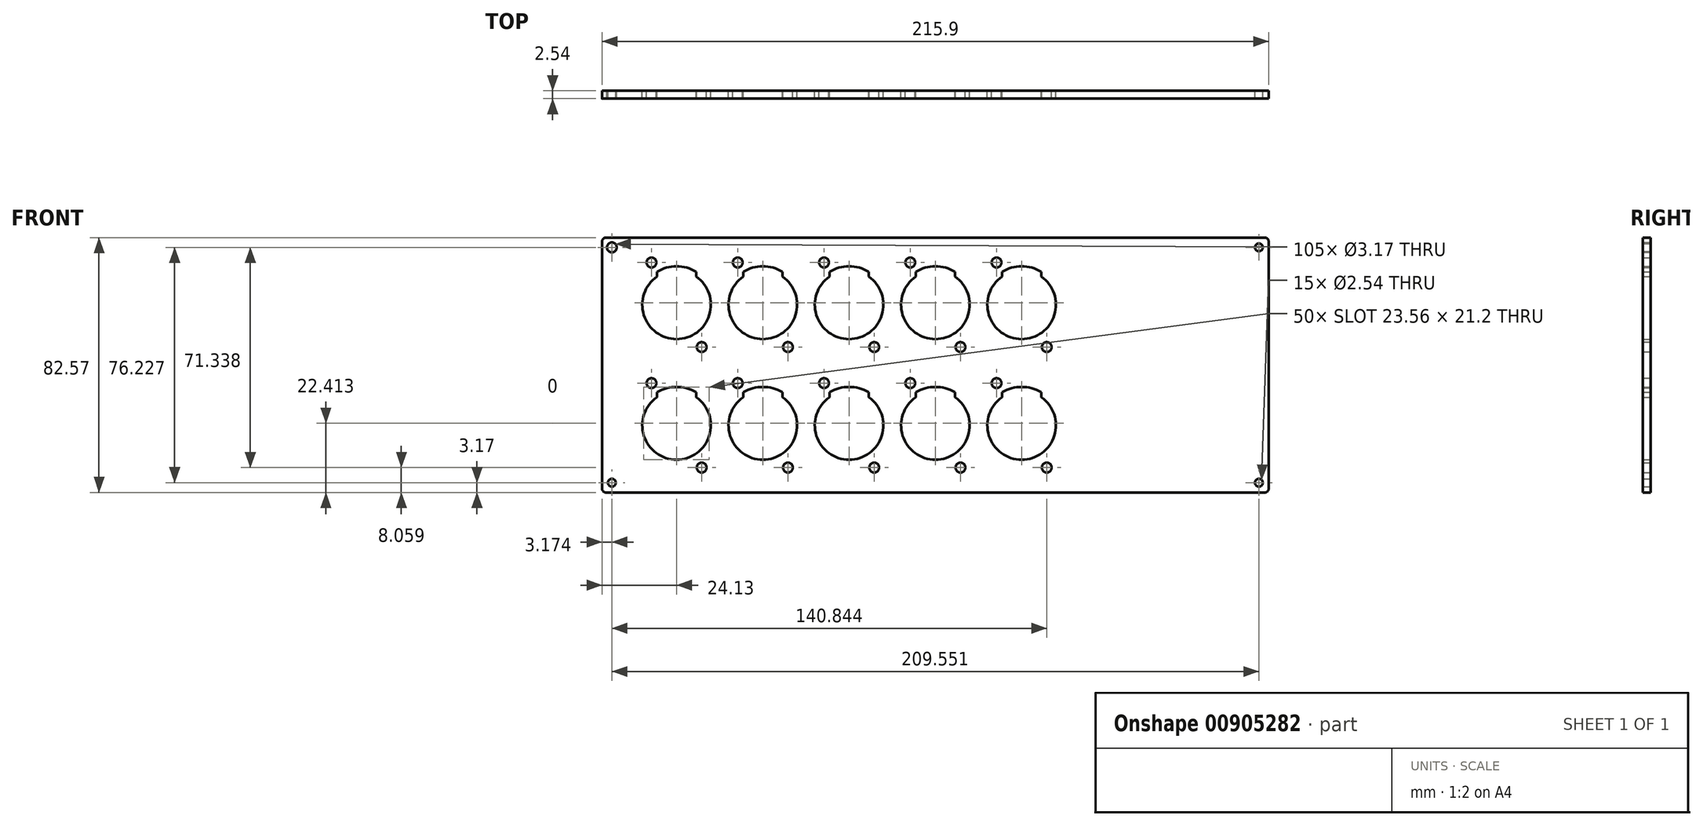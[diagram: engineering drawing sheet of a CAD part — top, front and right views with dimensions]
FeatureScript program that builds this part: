
annotation { "Feature Type Name" : "Feature", "Feature Type Description" : "" }
export const myFeature = defineFeature(function(context is Context, id is Id, definition is map)
    precondition{}
    {
        {
            var Q0;
            Q0=qCreatedBy(makeId("Front.planeOp"),FACE);
            var sketch = newSketch(context, id + "F0", { "sketchPlane" : qUnion([Q0])});
            skArc(sketch, "E0", {"start": v(-90.17, 28.65) * mm, "mid": v(-83.82, 8.41) * mm, "end": v(-77.47, 28.65) * mm});
            skPoint(sketch, "E0.centerSnap0", {"position": v(-71.12, 19.53) * mm});
            skPoint(sketch, "E0.centerSnap1", {"position": v(-83.82, 37.78) * mm});
            skCircle(sketch, "E1", {"center": v(-91.95, 33.21) * mm, "radius": 1.59 * mm});
            skCircle(sketch, "E2", {"center": v(-75.7, 5.84) * mm, "radius": 1.59 * mm});
            skArc(sketch, "E3", {"start": v(-77.47, 30.24) * mm, "mid": v(-83.82, 31.98) * mm, "end": v(-90.17, 30.24) * mm});
            skLineSegment(sketch, "E4", {"start": v(-90.17, 30.24) * mm, "end": v(-90.17, 28.65) * mm});
            skLineSegment(sketch, "E5", {"start": v(-77.47, 30.24) * mm, "end": v(-77.47, 28.65) * mm});
            skArc(sketch, "E6", {"start": v(-62.23, 28.65) * mm, "mid": v(-55.88, 8.41) * mm, "end": v(-49.53, 28.65) * mm});
            skPoint(sketch, "E6.centerSnap0", {"position": v(-43.18, 19.53) * mm});
            skPoint(sketch, "E6.centerSnap1", {"position": v(-55.88, 37.78) * mm});
            skCircle(sketch, "E7", {"center": v(-64, 33.21) * mm, "radius": 1.59 * mm});
            skCircle(sketch, "E8", {"center": v(-47.75, 5.84) * mm, "radius": 1.59 * mm});
            skArc(sketch, "E9", {"start": v(-49.53, 30.24) * mm, "mid": v(-55.88, 31.98) * mm, "end": v(-62.23, 30.24) * mm});
            skLineSegment(sketch, "E10", {"start": v(-62.23, 30.24) * mm, "end": v(-62.23, 28.65) * mm});
            skLineSegment(sketch, "E11", {"start": v(-49.53, 30.24) * mm, "end": v(-49.53, 28.65) * mm});
            skArc(sketch, "E12", {"start": v(-34.3, 28.65) * mm, "mid": v(-27.94, 8.41) * mm, "end": v(-21.59, 28.65) * mm});
            skPoint(sketch, "E12.centerSnap0", {"position": v(-15.24, 19.53) * mm});
            skPoint(sketch, "E12.centerSnap1", {"position": v(-27.94, 37.78) * mm});
            skCircle(sketch, "E13", {"center": v(-36.07, 33.21) * mm, "radius": 1.59 * mm});
            skCircle(sketch, "E14", {"center": v(-19.81, 5.84) * mm, "radius": 1.59 * mm});
            skArc(sketch, "E15", {"start": v(-21.59, 30.24) * mm, "mid": v(-27.94, 31.98) * mm, "end": v(-34.3, 30.24) * mm});
            skLineSegment(sketch, "E16", {"start": v(-34.3, 30.24) * mm, "end": v(-34.3, 28.65) * mm});
            skLineSegment(sketch, "E17", {"start": v(-21.6, 30.24) * mm, "end": v(-21.6, 28.65) * mm});
            skArc(sketch, "E18", {"start": v(-6.35, 28.65) * mm, "mid": v(0, 8.41) * mm, "end": v(6.35, 28.65) * mm});
            skPoint(sketch, "E18.centerSnap0", {"position": v(12.7, 19.53) * mm});
            skPoint(sketch, "E18.centerSnap1", {"position": v(0, 37.78) * mm});
            skCircle(sketch, "E19", {"center": v(-8.13, 33.21) * mm, "radius": 1.59 * mm});
            skCircle(sketch, "E20", {"center": v(8.13, 5.84) * mm, "radius": 1.59 * mm});
            skArc(sketch, "E21", {"start": v(6.35, 30.24) * mm, "mid": v(0, 31.98) * mm, "end": v(-6.35, 30.24) * mm});
            skLineSegment(sketch, "E22", {"start": v(-6.35, 30.24) * mm, "end": v(-6.35, 28.65) * mm});
            skLineSegment(sketch, "E23", {"start": v(6.35, 30.24) * mm, "end": v(6.35, 28.65) * mm});
            skArc(sketch, "E24", {"start": v(21.6, 28.65) * mm, "mid": v(27.94, 8.41) * mm, "end": v(34.3, 28.65) * mm});
            skPoint(sketch, "E24.centerSnap0", {"position": v(40.64, 19.53) * mm});
            skPoint(sketch, "E24.centerSnap1", {"position": v(27.94, 37.78) * mm});
            skCircle(sketch, "E25", {"center": v(19.81, 33.21) * mm, "radius": 1.59 * mm});
            skCircle(sketch, "E26", {"center": v(36.07, 5.84) * mm, "radius": 1.59 * mm});
            skArc(sketch, "E27", {"start": v(34.3, 30.24) * mm, "mid": v(27.94, 31.98) * mm, "end": v(21.6, 30.24) * mm});
            skLineSegment(sketch, "E28", {"start": v(21.6, 30.24) * mm, "end": v(21.6, 28.65) * mm});
            skLineSegment(sketch, "E29", {"start": v(34.3, 30.24) * mm, "end": v(34.3, 28.65) * mm});
            skArc(sketch, "E30", {"start": v(-90.17, -10.4) * mm, "mid": v(-83.82, -30.64) * mm, "end": v(-77.47, -10.4) * mm});
            skPoint(sketch, "E30.centerSnap0", {"position": v(-71.12, -19.53) * mm});
            skPoint(sketch, "E30.centerSnap1", {"position": v(-83.82, -1.27) * mm});
            skCircle(sketch, "E31", {"center": v(-91.95, -5.84) * mm, "radius": 1.59 * mm});
            skCircle(sketch, "E32", {"center": v(-75.7, -33.21) * mm, "radius": 1.59 * mm});
            skArc(sketch, "E33", {"start": v(-77.47, -8.82) * mm, "mid": v(-83.82, -7.08) * mm, "end": v(-90.17, -8.82) * mm});
            skLineSegment(sketch, "E34", {"start": v(-90.17, -8.82) * mm, "end": v(-90.17, -10.4) * mm});
            skLineSegment(sketch, "E35", {"start": v(-77.47, -8.82) * mm, "end": v(-77.47, -10.4) * mm});
            skArc(sketch, "E36", {"start": v(-62.23, -10.4) * mm, "mid": v(-55.88, -30.64) * mm, "end": v(-49.53, -10.4) * mm});
            skPoint(sketch, "E36.centerSnap0", {"position": v(-43.18, -19.53) * mm});
            skPoint(sketch, "E36.centerSnap1", {"position": v(-55.88, -1.27) * mm});
            skCircle(sketch, "E37", {"center": v(-64, -5.84) * mm, "radius": 1.59 * mm});
            skCircle(sketch, "E38", {"center": v(-47.75, -33.21) * mm, "radius": 1.59 * mm});
            skArc(sketch, "E39", {"start": v(-49.53, -8.82) * mm, "mid": v(-55.88, -7.08) * mm, "end": v(-62.23, -8.82) * mm});
            skLineSegment(sketch, "E40", {"start": v(-62.23, -8.82) * mm, "end": v(-62.23, -10.4) * mm});
            skLineSegment(sketch, "E41", {"start": v(-49.53, -8.82) * mm, "end": v(-49.53, -10.4) * mm});
            skArc(sketch, "E42", {"start": v(-34.3, -10.4) * mm, "mid": v(-27.94, -30.64) * mm, "end": v(-21.6, -10.4) * mm});
            skPoint(sketch, "E42.centerSnap0", {"position": v(-15.24, -19.53) * mm});
            skPoint(sketch, "E42.centerSnap1", {"position": v(-27.94, -1.27) * mm});
            skCircle(sketch, "E43", {"center": v(-36.07, -5.84) * mm, "radius": 1.59 * mm});
            skCircle(sketch, "E44", {"center": v(-19.81, -33.21) * mm, "radius": 1.59 * mm});
            skArc(sketch, "E45", {"start": v(-21.6, -8.82) * mm, "mid": v(-27.94, -7.08) * mm, "end": v(-34.3, -8.82) * mm});
            skLineSegment(sketch, "E46", {"start": v(-34.3, -8.82) * mm, "end": v(-34.3, -10.4) * mm});
            skLineSegment(sketch, "E47", {"start": v(-21.6, -8.82) * mm, "end": v(-21.59, -10.4) * mm});
            skArc(sketch, "E48", {"start": v(-6.35, -10.4) * mm, "mid": v(0, -30.64) * mm, "end": v(6.35, -10.4) * mm});
            skPoint(sketch, "E48.centerSnap0", {"position": v(12.7, -19.53) * mm});
            skPoint(sketch, "E48.centerSnap1", {"position": v(0, -1.27) * mm});
            skCircle(sketch, "E49", {"center": v(-8.13, -5.84) * mm, "radius": 1.59 * mm});
            skCircle(sketch, "E50", {"center": v(8.13, -33.21) * mm, "radius": 1.59 * mm});
            skArc(sketch, "E51", {"start": v(6.35, -8.82) * mm, "mid": v(0, -7.08) * mm, "end": v(-6.35, -8.82) * mm});
            skLineSegment(sketch, "E52", {"start": v(-6.35, -8.82) * mm, "end": v(-6.35, -10.4) * mm});
            skLineSegment(sketch, "E53", {"start": v(6.35, -8.82) * mm, "end": v(6.35, -10.4) * mm});
            skArc(sketch, "E54", {"start": v(21.6, -10.4) * mm, "mid": v(27.94, -30.64) * mm, "end": v(34.3, -10.4) * mm});
            skPoint(sketch, "E54.centerSnap0", {"position": v(40.64, -19.53) * mm});
            skPoint(sketch, "E54.centerSnap1", {"position": v(27.94, -1.27) * mm});
            skCircle(sketch, "E55", {"center": v(19.81, -5.84) * mm, "radius": 1.59 * mm});
            skCircle(sketch, "E56", {"center": v(36.07, -33.21) * mm, "radius": 1.59 * mm});
            skArc(sketch, "E57", {"start": v(34.3, -8.82) * mm, "mid": v(27.94, -7.08) * mm, "end": v(21.6, -8.82) * mm});
            skLineSegment(sketch, "E58", {"start": v(21.6, -8.82) * mm, "end": v(21.6, -10.4) * mm});
            skLineSegment(sketch, "E59", {"start": v(34.3, -8.82) * mm, "end": v(34.3, -10.4) * mm});
            skLineSegment(sketch, "E60.bottom", {"start": v(-106.68, 41.3) * mm, "end": v(106.68, 41.3) * mm});
            skLineSegment(sketch, "E60.top", {"start": v(-106.68, -41.28) * mm, "end": v(106.68, -41.28) * mm});
            skLineSegment(sketch, "E60.left", {"start": v(-107.95, 40.03) * mm, "end": v(-107.95, -40) * mm});
            skLineSegment(sketch, "E60.right", {"start": v(107.95, 40.03) * mm, "end": v(107.95, -40) * mm});
            skArc(sketch, "E61", {"start": v(-106.68, 41.3) * mm, "mid": v(-107.58, 40.93) * mm, "end": v(-107.95, 40.03) * mm});
            skArc(sketch, "E62", {"start": v(-107.95, -40) * mm, "mid": v(-107.58, -40.9) * mm, "end": v(-106.68, -41.28) * mm});
            skArc(sketch, "E63", {"start": v(106.68, -41.28) * mm, "mid": v(107.58, -40.9) * mm, "end": v(107.95, -40) * mm});
            skArc(sketch, "E64", {"start": v(107.95, 40.03) * mm, "mid": v(107.58, 40.93) * mm, "end": v(106.68, 41.3) * mm});
            skCircle(sketch, "E65", {"center": v(104.78, 38.13) * mm, "radius": 1.27 * mm});
            skCircle(sketch, "E66", {"center": v(104.78, -38.1) * mm, "radius": 1.27 * mm});
            skCircle(sketch, "E67", {"center": v(-104.78, 38.13) * mm, "radius": 1.59 * mm});
            skCircle(sketch, "E68", {"center": v(-104.78, -38.1) * mm, "radius": 1.27 * mm});
            skSolve(sketch);
        }
        {
            var Q0;
            Q0=makeQuery(id+"F0.imprint","IMPRINT",FACE,{"disambiguationData":[TD([[makeQuery(id+"F0.imprint","IMPRINT",EDGE,{"derivedFrom":sQuery(id+"F0.wireOp",EDGE,"E0")}),-1.0]])]});
            extrude(context, id + "F1", {"entities" : qUnion([Q0]), "depth" : 2.54 * mm, "offsetDistance" : 25.4 * mm});
        }
    });
